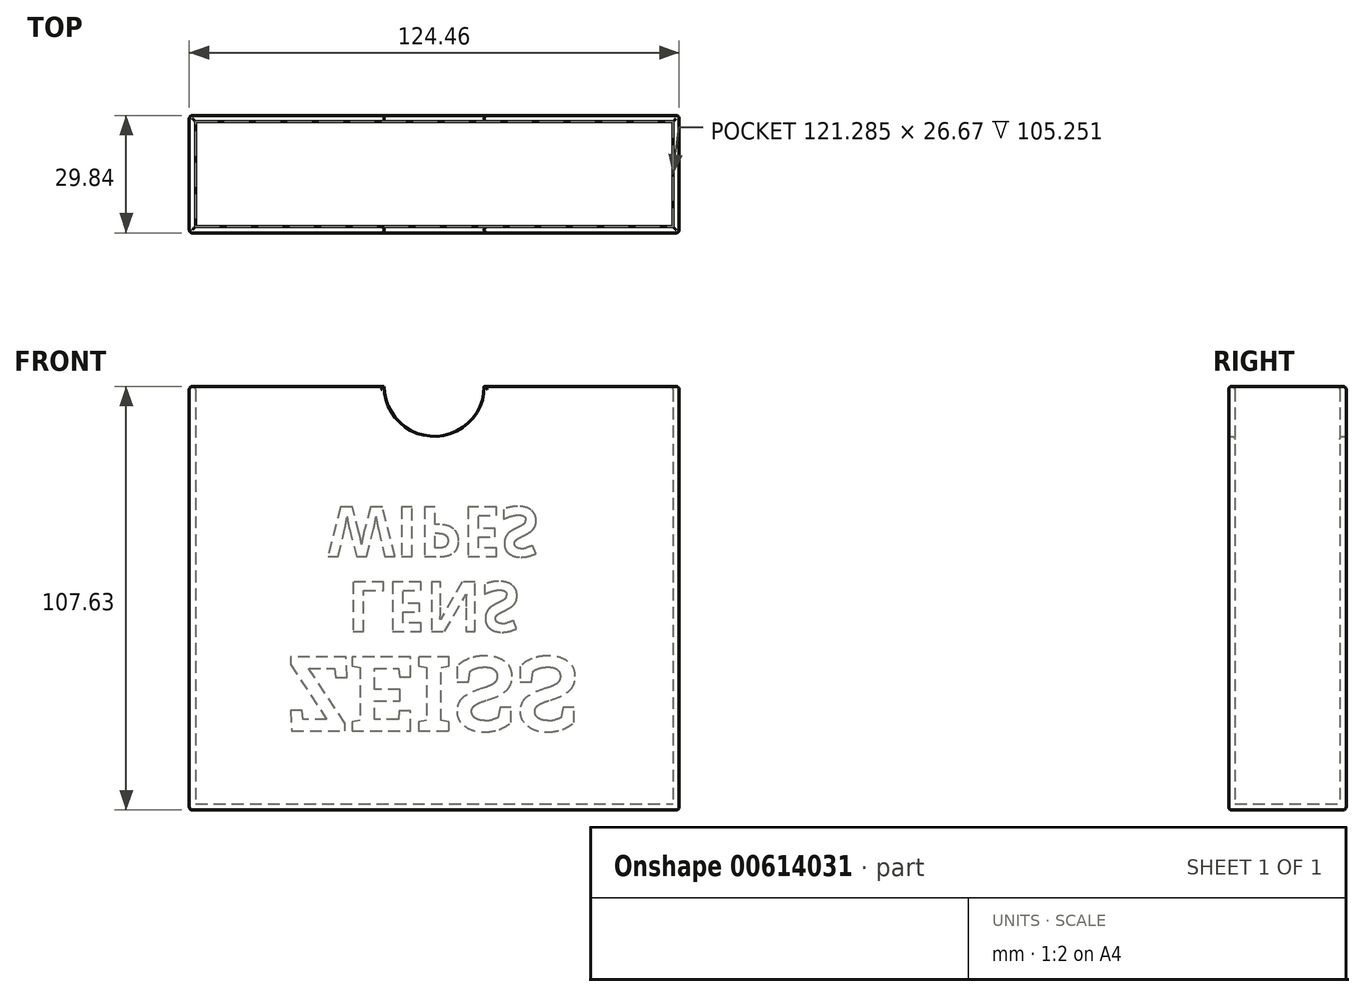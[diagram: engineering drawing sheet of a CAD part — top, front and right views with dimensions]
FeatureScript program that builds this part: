
annotation { "Feature Type Name" : "Feature", "Feature Type Description" : "" }
export const myFeature = defineFeature(function(context is Context, id is Id, definition is map)
    precondition{}
    {
        {
            var Q0;
            Q0=qCreatedBy(makeId("Top.planeOp"),FACE);
            var sketch = newSketch(context, id + "F0", { "sketchPlane" : qUnion([Q0])});
            skLineSegment(sketch, "E0.bottom", {"start": v(-62.23, -14.92) * mm, "end": v(62.23, -14.92) * mm});
            skLineSegment(sketch, "E0.top", {"start": v(-62.23, 14.92) * mm, "end": v(62.23, 14.92) * mm});
            skLineSegment(sketch, "E0.left", {"start": v(-62.23, -14.92) * mm, "end": v(-62.23, 14.92) * mm});
            skLineSegment(sketch, "E0.right", {"start": v(62.23, -14.92) * mm, "end": v(62.23, 14.92) * mm});
            skPoint(sketch, "E0.middle", {"position": v(0, 0) * mm});
            skSolve(sketch);
        }
        {
            var Q0;
            Q0=makeQuery(id+"F0.imprint","IMPRINT",FACE,{"disambiguationData":[TD([[makeQuery(id+"F0.imprint","IMPRINT",EDGE,{"derivedFrom":sQuery(id+"F0.wireOp",EDGE,"E0.bottom")}),1.0]])]});
            extrude(context, id + "F1", {"entities" : qUnion([Q0]), "depth" : 107.63 * mm, "offsetDistance" : 25.4 * mm});
        }
        {
            var Q0;
            Q0=makeQuery(id+"F1.opExtrude","CAP_FACE",FACE,{"disambiguationData":[OSD([sQuery(id+"F0.wireOp",EDGE,"E0.bottom"),sQuery(id+"F0.wireOp",EDGE,"E0.top"),sQuery(id+"F0.wireOp",EDGE,"E0.left"),sQuery(id+"F0.wireOp",EDGE,"E0.right")])],"isStart":false});
            shell(context, id + "F2", {"entities" : qUnion([Q0]), "thickness" : 1.59 * mm});
        }
        {
            var Q0;
            Q0=makeQuery(id+"F1.opExtrude","SWEPT_FACE",FACE,{"disambiguationData":[OSD([sQuery(id+"F0.wireOp",EDGE,"E0.bottom")])]});
            var sketch = newSketch(context, id + "F3", { "sketchPlane" : qUnion([Q0])});
            skCircle(sketch, "E1", {"center": v(0, 107.63) * mm, "radius": 12.7 * mm});
            skSolve(sketch);
        }
        {
            var Q0;
            {var subQ0=sQuery(id+"F3.wireOp",EDGE,"E1");var subQ1=makeQuery(id+"F1.opExtrude","CAP_EDGE",EDGE,{"disambiguationData":[OSD([sQuery(id+"F0.wireOp",EDGE,"E0.bottom")])],"isStart":false});var subQ2=makeQuery(id+"F3.imprint","INTERSECT",VERTEX,{"disambiguationData":[OD(0.0)],"derivedFrom":[subQ1,subQ0]});Q0=makeQuery(id+"F3.imprint","IMPRINT",FACE,{"disambiguationData":[TD([[makeQuery(id+"F3.imprint","IMPRINT",EDGE,{"disambiguationData":[TD([[subQ2,-1.0]])],"derivedFrom":subQ0}),1.0]])]});}
            extrude(context, id + "F4", {"entities" : qUnion([Q0]), "operationType" : NewBodyOperationType.REMOVE, "endBound" : BoundingType.THROUGH_ALL, "oppositeDirection" : true, "depth" : 25.4 * mm, "offsetDistance" : 25.4 * mm});
        }
        {
            var Q0;
            Q0=makeQuery(id+"F1.opExtrude","SWEPT_FACE",FACE,{"disambiguationData":[OSD([sQuery(id+"F0.wireOp",EDGE,"E0.bottom")])]});
            var Q1;
            Q1=makeQuery(id+"F1.opExtrude","SWEPT_FACE",FACE,{"disambiguationData":[OSD([sQuery(id+"F0.wireOp",EDGE,"E0.left")])]});
            var Q2;
            Q2=makeQuery(id+"F1.opExtrude","SWEPT_FACE",FACE,{"disambiguationData":[OSD([sQuery(id+"F0.wireOp",EDGE,"E0.right")])]});
            var Q3;
            Q3=makeQuery(id+"F1.opExtrude","SWEPT_FACE",FACE,{"disambiguationData":[OSD([sQuery(id+"F0.wireOp",EDGE,"E0.top")])]});
            var Q4;
            {var subQ0=sQuery(id+"F0.wireOp",EDGE,"E0.left");var subQ1=sQuery(id+"F0.wireOp",EDGE,"E0.bottom");Q4=makeQuery(id+"F4.boolean.opBoolean","SPLIT",EDGE,{"disambiguationData":[TD([makeQuery(id+"F2.opShell","OFFSET_FACE",FACE,{"disambiguationData":[OSD([subQ0])]})])],"derivedFrom":makeQuery(id+"F2.opShell","OFFSET_EDGE",EDGE,{"disambiguationData":[OSD([subQ1]),TDD([makeQuery(id+"F1.opExtrude","CAP_EDGE",EDGE,{"disambiguationData":[OSD([subQ1])],"isStart":false})])]})});}
            var Q5;
            {var subQ0=sQuery(id+"F0.wireOp",EDGE,"E0.left");Q5=makeQuery(id+"F2.opShell","OFFSET_EDGE",EDGE,{"disambiguationData":[OSD([subQ0]),TDD([makeQuery(id+"F1.opExtrude","CAP_EDGE",EDGE,{"disambiguationData":[OSD([subQ0])],"isStart":false})])]});}
            var Q6;
            {var subQ0=sQuery(id+"F0.wireOp",EDGE,"E0.left");var subQ1=sQuery(id+"F0.wireOp",EDGE,"E0.top");Q6=makeQuery(id+"F4.boolean.opBoolean","SPLIT",EDGE,{"disambiguationData":[TD([makeQuery(id+"F2.opShell","OFFSET_FACE",FACE,{"disambiguationData":[OSD([subQ0])]})])],"derivedFrom":makeQuery(id+"F2.opShell","OFFSET_EDGE",EDGE,{"disambiguationData":[OSD([subQ1]),TDD([makeQuery(id+"F1.opExtrude","CAP_EDGE",EDGE,{"disambiguationData":[OSD([subQ1])],"isStart":false})])]})});}
            var Q7;
            Q7=makeQuery(id+"F4.boolean.opBoolean","INTERSECT",EDGE,{"derivedFrom":[makeQuery(id+"F2.opShell","OFFSET_FACE",FACE,{"disambiguationData":[OSD([sQuery(id+"F0.wireOp",EDGE,"E0.top")])]}),makeQuery(id+"F4.opExtrude","SWEPT_FACE",FACE,{"disambiguationData":[OSD([sQuery(id+"F3.wireOp",EDGE,"E1")])]})]});
            var Q8;
            Q8=makeQuery(id+"F4.boolean.opBoolean","INTERSECT",EDGE,{"derivedFrom":[makeQuery(id+"F2.opShell","OFFSET_FACE",FACE,{"disambiguationData":[OSD([sQuery(id+"F0.wireOp",EDGE,"E0.bottom")])]}),makeQuery(id+"F4.opExtrude","SWEPT_FACE",FACE,{"disambiguationData":[OSD([sQuery(id+"F3.wireOp",EDGE,"E1")])]})]});
            var Q9;
            {var subQ0=sQuery(id+"F0.wireOp",EDGE,"E0.right");var subQ1=sQuery(id+"F0.wireOp",EDGE,"E0.bottom");Q9=makeQuery(id+"F4.boolean.opBoolean","SPLIT",EDGE,{"disambiguationData":[TD([makeQuery(id+"F2.opShell","OFFSET_FACE",FACE,{"disambiguationData":[OSD([subQ0])]})])],"derivedFrom":makeQuery(id+"F2.opShell","OFFSET_EDGE",EDGE,{"disambiguationData":[OSD([subQ1]),TDD([makeQuery(id+"F1.opExtrude","CAP_EDGE",EDGE,{"disambiguationData":[OSD([subQ1])],"isStart":false})])]})});}
            var Q10;
            {var subQ0=sQuery(id+"F0.wireOp",EDGE,"E0.right");var subQ1=sQuery(id+"F0.wireOp",EDGE,"E0.top");Q10=makeQuery(id+"F4.boolean.opBoolean","SPLIT",EDGE,{"disambiguationData":[TD([makeQuery(id+"F2.opShell","OFFSET_FACE",FACE,{"disambiguationData":[OSD([subQ0])]})])],"derivedFrom":makeQuery(id+"F2.opShell","OFFSET_EDGE",EDGE,{"disambiguationData":[OSD([subQ1]),TDD([makeQuery(id+"F1.opExtrude","CAP_EDGE",EDGE,{"disambiguationData":[OSD([subQ1])],"isStart":false})])]})});}
            var Q11;
            {var subQ0=sQuery(id+"F0.wireOp",EDGE,"E0.right");Q11=makeQuery(id+"F2.opShell","OFFSET_EDGE",EDGE,{"disambiguationData":[OSD([subQ0]),TDD([makeQuery(id+"F1.opExtrude","CAP_EDGE",EDGE,{"disambiguationData":[OSD([subQ0])],"isStart":false})])]});}
            fillet(context, id + "F5", {"entities" : qUnion([Q0, Q1, Q2, Q3, Q4, Q5, Q6, Q7, Q8, Q9, Q10, Q11]), "radius" : 0.8 * mm, "tangentPropagation" : true, "allowEdgeOverflow" : false});
        }
        {
            var Q0;
            Q0=makeQuery(id+"F1.opExtrude","SWEPT_FACE",FACE,{"disambiguationData":[OSD([sQuery(id+"F0.wireOp",EDGE,"E0.top")])]});
            var sketch = newSketch(context, id + "F6", { "sketchPlane" : qUnion([Q0])});
            skText(sketch, "E2", { "text": "ZEISS", "fontName": "RobotoSlab-Bold.ttf"});
            skText(sketch, "E3", { "text": "LENS", "fontName": "OpenSans-Bold.ttf"});
            skText(sketch, "E4", { "text": "WIPES", "fontName": "OpenSans-Bold.ttf"});
            const initialGuessF6  = {"E2": [0.03745, 0.0389, -1, 0, 0.01905], "E3": [0.02217, 0.05794, -1, 0, 0.0127], "E4": [0.027, 0.077, -1, 0, 0.0127]};
            skSetInitialGuess(sketch, initialGuessF6);
            skSolve(sketch);
        }
        {
            var Q0;
            Q0 = qSketchRegion(id + "F6", true);
            extrude(context, id + "F7", {"entities" : qUnion([Q0]), "operationType" : NewBodyOperationType.REMOVE, "oppositeDirection" : true, "depth" : 0.13 * mm, "offsetDistance" : 25.4 * mm});
        }
    });
